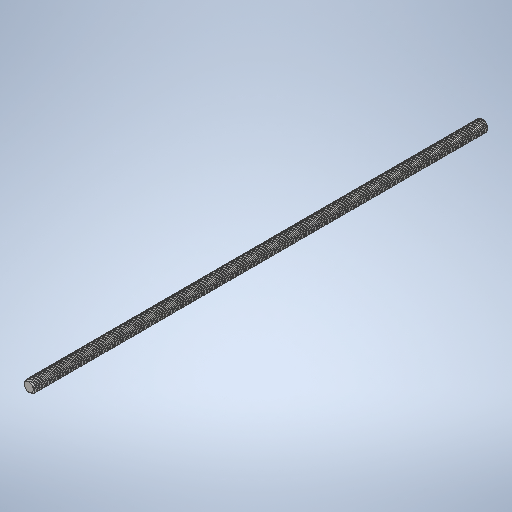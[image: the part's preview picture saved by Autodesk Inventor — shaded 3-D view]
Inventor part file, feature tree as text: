
AUTODESK INVENTOR PART (.ipt)
format: ipt  version: 2025.2 (Build 292293000, 293)  size: 1,363,456 bytes
history: native  units: mm
features: extrude x1, chamfer x1, other x1, pattern_circular x1
ambient origin geometry x8: Origin, YZ Plane, XZ Plane, XY Plane, X Axis, Y Axis, Z Axis, Center Point
bodies: Solid1 (feature_tree)
feature tree (4):
  extrude  "1000mm Rod"  Depth=315.0mm TaperAngle=0.0deg
  chamfer  "Chamfer1"  Distance=0.907143mm Angle=45.0deg
  other  "ACME Thread 2mm Pitch"
  pattern_circular  "4 Start"  [2 undecoded]
note: 2 required parameter values undecoded (feature->parameter linkage not recoverable at this tier; creation-order binding heuristic only, values carry confidence <= 0.55)
